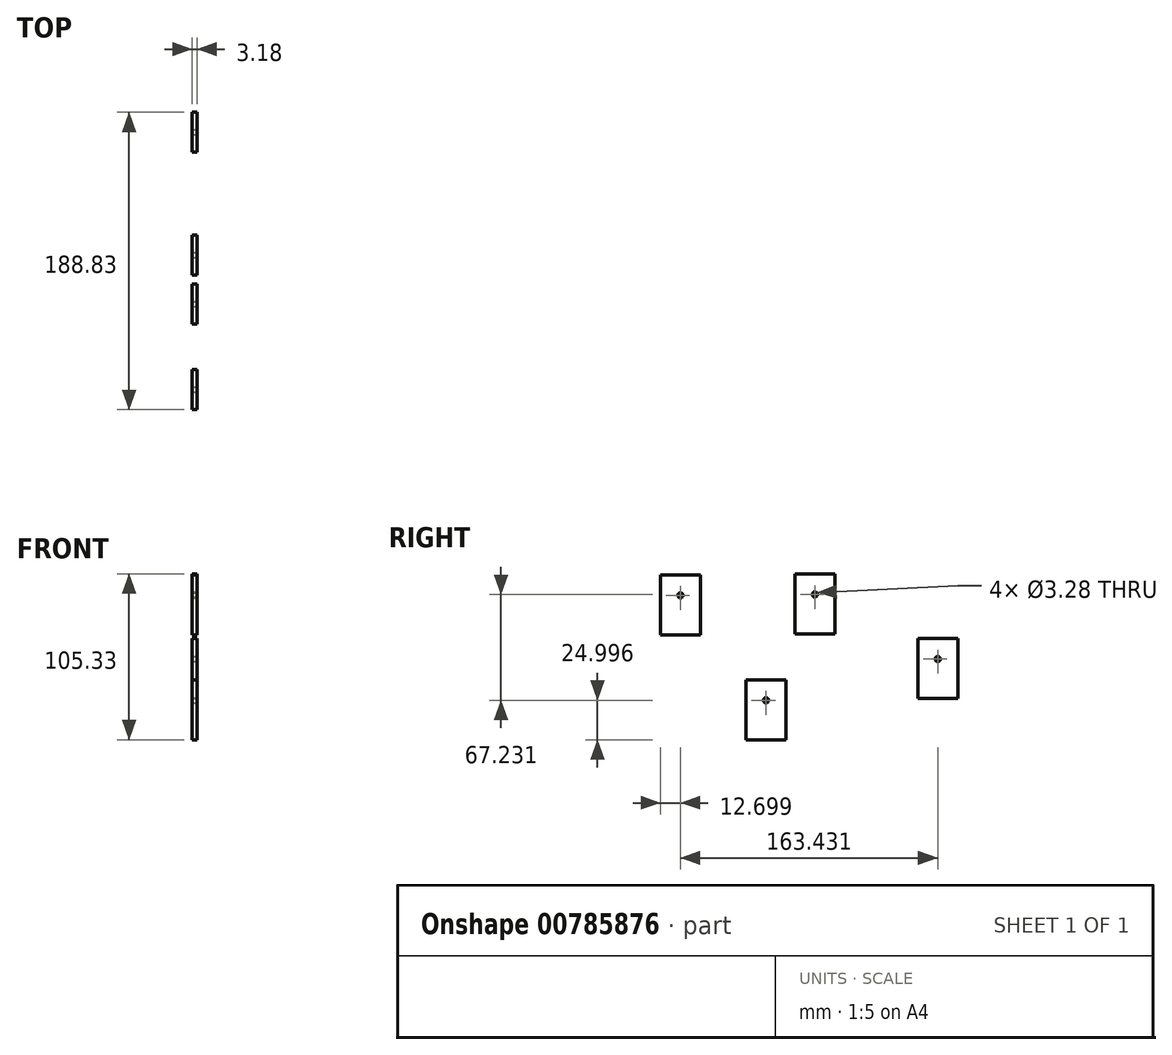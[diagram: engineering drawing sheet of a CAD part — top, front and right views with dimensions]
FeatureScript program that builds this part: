
annotation { "Feature Type Name" : "Feature", "Feature Type Description" : "" }
export const myFeature = defineFeature(function(context is Context, id is Id, definition is map)
    precondition{}
    {
        {
            var Q0;
            Q0=qCreatedBy(makeId("Right.planeOp"),FACE);
            var sketch = newSketch(context, id + "F0", { "sketchPlane" : qUnion([Q0])});
            skLineSegment(sketch, "E0.bottom", {"start": v(-39.14, 38.67) * mm, "end": v(-13.74, 38.67) * mm});
            skLineSegment(sketch, "E0.top", {"start": v(-39.14, 0.57) * mm, "end": v(-13.74, 0.57) * mm});
            skLineSegment(sketch, "E0.left", {"start": v(-39.14, 38.67) * mm, "end": v(-39.14, 0.57) * mm});
            skLineSegment(sketch, "E0.right", {"start": v(-13.74, 38.67) * mm, "end": v(-13.74, 0.57) * mm});
            skPoint(sketch, "E1.positionSnap0", {"position": v(-13.74, 19.62) * mm});
            skPoint(sketch, "E1.positionSnap1", {"position": v(-26.44, 38.67) * mm});
            skCircle(sketch, "E2", {"center": v(-26.44, 25.57) * mm, "radius": 1.64 * mm});
            skLineSegment(sketch, "E3.bottom", {"start": v(38.9, -2.36) * mm, "end": v(64.3, -2.36) * mm});
            skLineSegment(sketch, "E3.top", {"start": v(38.9, -40.46) * mm, "end": v(64.3, -40.46) * mm});
            skLineSegment(sketch, "E3.left", {"start": v(38.9, -2.36) * mm, "end": v(38.9, -40.46) * mm});
            skLineSegment(sketch, "E3.right", {"start": v(64.3, -2.36) * mm, "end": v(64.3, -40.46) * mm});
            skPoint(sketch, "E4.positionSnap0", {"position": v(64.3, -21.41) * mm});
            skPoint(sketch, "E4.positionSnap1", {"position": v(51.6, -2.36) * mm});
            skCircle(sketch, "E5", {"center": v(51.6, -15.46) * mm, "radius": 1.64 * mm});
            skLineSegment(sketch, "E6.bottom", {"start": v(-124.53, 38.1) * mm, "end": v(-99.13, 38.1) * mm});
            skLineSegment(sketch, "E6.top", {"start": v(-124.53, 0) * mm, "end": v(-99.13, 0) * mm});
            skLineSegment(sketch, "E6.left", {"start": v(-124.53, 38.1) * mm, "end": v(-124.53, 0) * mm});
            skLineSegment(sketch, "E6.right", {"start": v(-99.13, 38.1) * mm, "end": v(-99.13, 0) * mm});
            skPoint(sketch, "E7.positionSnap0", {"position": v(-99.13, 19.05) * mm});
            skPoint(sketch, "E7.positionSnap1", {"position": v(-111.83, 38.1) * mm});
            skCircle(sketch, "E8", {"center": v(-111.83, 25) * mm, "radius": 1.64 * mm});
            skLineSegment(sketch, "E9.bottom", {"start": v(-70.15, -28.56) * mm, "end": v(-44.75, -28.56) * mm});
            skLineSegment(sketch, "E9.top", {"start": v(-70.15, -66.66) * mm, "end": v(-44.75, -66.66) * mm});
            skLineSegment(sketch, "E9.left", {"start": v(-70.15, -28.56) * mm, "end": v(-70.15, -66.66) * mm});
            skLineSegment(sketch, "E9.right", {"start": v(-44.75, -28.56) * mm, "end": v(-44.75, -66.66) * mm});
            skPoint(sketch, "E10.positionSnap0", {"position": v(-44.75, -47.61) * mm});
            skPoint(sketch, "E10.positionSnap1", {"position": v(-57.45, -28.56) * mm});
            skCircle(sketch, "E11", {"center": v(-57.45, -41.66) * mm, "radius": 1.64 * mm});
            skSolve(sketch);
        }
        {
            var Q0;
            Q0=makeQuery(id+"F0.imprint","IMPRINT",FACE,{"disambiguationData":[TD([[makeQuery(id+"F0.imprint","IMPRINT",EDGE,{"derivedFrom":sQuery(id+"F0.wireOp",EDGE,"E0.bottom")}),-1.0]])]});
            extrude(context, id + "F1", {"entities" : qUnion([Q0]), "oppositeDirection" : true, "depth" : 3.17 * mm, "offsetDistance" : 25.4 * mm});
        }
        {
            var Q0;
            Q0=makeQuery(id+"F0.imprint","IMPRINT",FACE,{"disambiguationData":[TD([[makeQuery(id+"F0.imprint","IMPRINT",EDGE,{"derivedFrom":sQuery(id+"F0.wireOp",EDGE,"E3.bottom")}),-1.0]])]});
            extrude(context, id + "F2", {"entities" : qUnion([Q0]), "oppositeDirection" : true, "depth" : 3.17 * mm, "offsetDistance" : 25.4 * mm});
        }
        {
            var Q0;
            Q0=makeQuery(id+"F0.imprint","IMPRINT",FACE,{"disambiguationData":[TD([[makeQuery(id+"F0.imprint","IMPRINT",EDGE,{"derivedFrom":sQuery(id+"F0.wireOp",EDGE,"E6.bottom")}),-1.0]])]});
            extrude(context, id + "F3", {"entities" : qUnion([Q0]), "oppositeDirection" : true, "depth" : 3.17 * mm, "offsetDistance" : 25.4 * mm});
        }
        {
            var Q0;
            Q0=makeQuery(id+"F0.imprint","IMPRINT",FACE,{"disambiguationData":[TD([[makeQuery(id+"F0.imprint","IMPRINT",EDGE,{"derivedFrom":sQuery(id+"F0.wireOp",EDGE,"E9.bottom")}),-1.0]])]});
            extrude(context, id + "F4", {"entities" : qUnion([Q0]), "oppositeDirection" : true, "depth" : 3.17 * mm, "offsetDistance" : 25.4 * mm});
        }
    });
